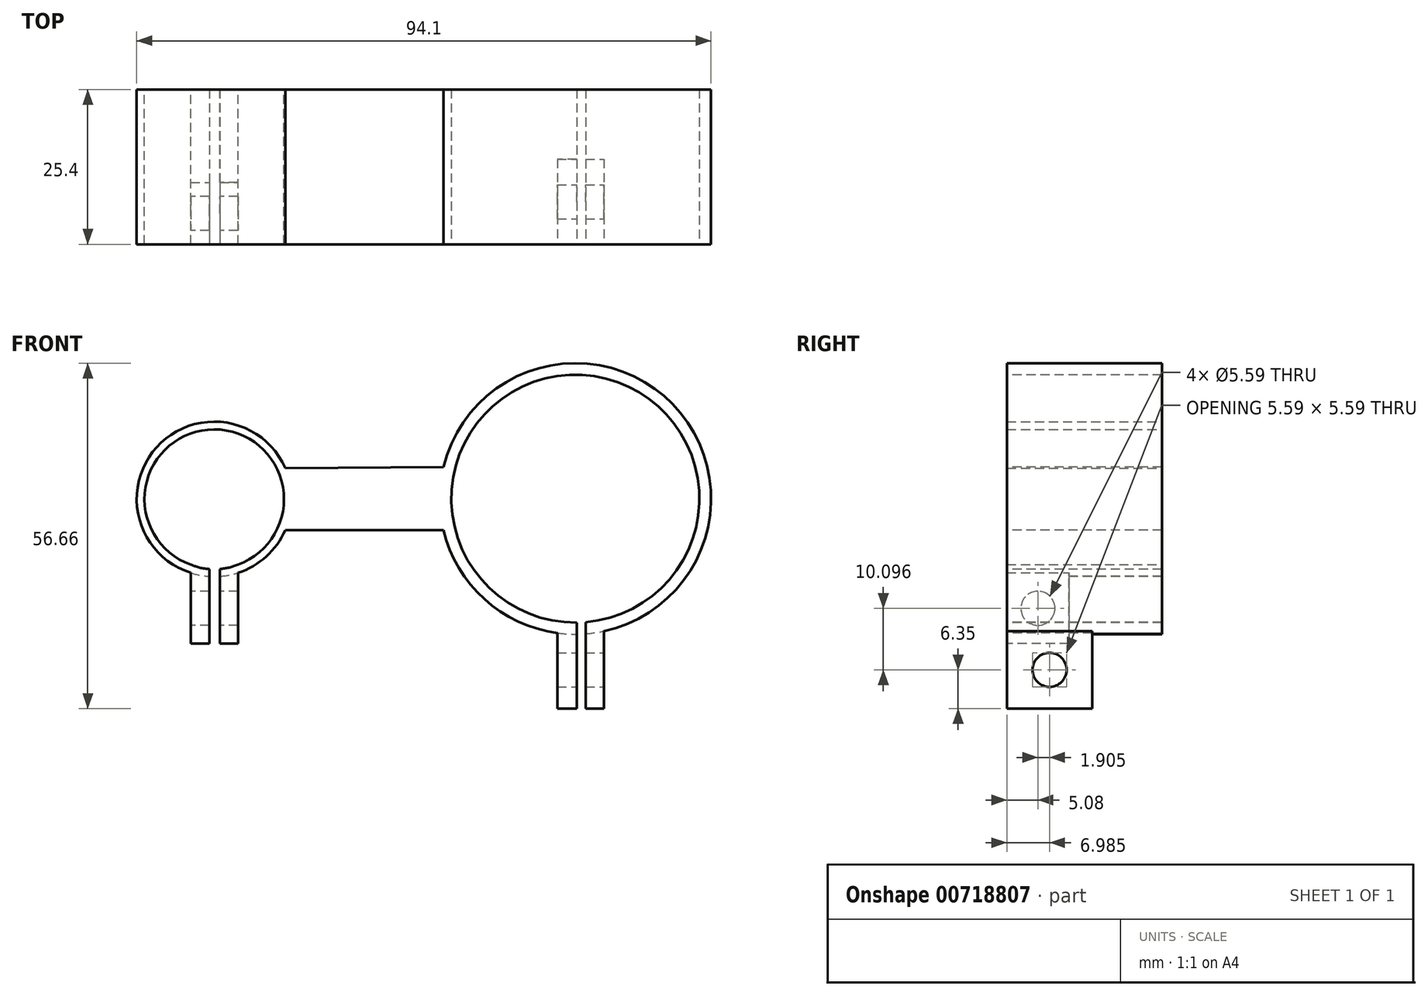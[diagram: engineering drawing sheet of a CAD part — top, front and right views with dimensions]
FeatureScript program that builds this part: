
annotation { "Feature Type Name" : "Feature", "Feature Type Description" : "" }
export const myFeature = defineFeature(function(context is Context, id is Id, definition is map)
    precondition{}
    {
        {
            var Q0;
            Q0=qCreatedBy(makeId("Front.planeOp"),FACE);
            var sketch = newSketch(context, id + "F0", { "sketchPlane" : qUnion([Q0])});
            skCircle(sketch, "E0", {"center": v(0, 0) * mm, "radius": 12.7 * mm});
            skCircle(sketch, "E1", {"center": v(0, 0) * mm, "radius": 11.43 * mm});
            skSolve(sketch);
        }
        {
            var Q0;
            Q0 = qSketchRegion(id + "F0", true);
            extrude(context, id + "F1", {"entities" : qUnion([Q0]), "depth" : 25.4 * mm, "offsetDistance" : 25.4 * mm});
        }
        {
            var Q0;
            Q0=qCreatedBy(makeId("Front.planeOp"),FACE);
            cPlane(context, id + "F2", {"entities" : qUnion([Q0]), "cplaneType" : CPlaneType.OFFSET, "offset" : 25.4 * mm, "width" : 152.4 * mm, "height" : 152.4 * mm});
        }
        {
            var Q0;
            Q0=qCreatedBy(id+"F2.planeOp",FACE);
            var sketch = newSketch(context, id + "F3", { "sketchPlane" : qUnion([Q0])});
            skLineSegment(sketch, "E2", {"start": v(10.6, 5.08) * mm, "end": v(38.72, 5.3) * mm});
            skLineSegment(sketch, "E3", {"start": v(38.68, -5.08) * mm, "end": v(10.4, -5.08) * mm});
            skArc(sketch, "E4", {"start": v(10.4, -5.08) * mm, "mid": v(11.82, -0.02) * mm, "end": v(10.6, 5.08) * mm});
            skPoint(sketch, "E5.orphan", {"position": v(0, -5.08) * mm});
            skArc(sketch, "E6", {"start": v(38.72, 5.3) * mm, "mid": v(37.32, 0.11) * mm, "end": v(38.68, -5.08) * mm});
            skPoint(sketch, "E7.orphan", {"position": v(48.12, -5.08) * mm});
            skLineSegment(sketch, "E8", {"start": v(0, 0) * mm, "end": v(36.95, 0.04) * mm});
            skCircle(sketch, "E9", {"center": v(59.18, 0.07) * mm, "radius": 22.23 * mm});
            skLineSegment(sketch, "E10", {"start": v(37.57, 5.28) * mm, "end": v(38.72, 5.3) * mm});
            skCircle(sketch, "E11", {"center": v(59.18, 0.07) * mm, "radius": 20.32 * mm});
            skSolve(sketch);
        }
        {
            var Q0;
            Q0 = qSketchRegion(id + "F3", true);
            extrude(context, id + "F4", {"entities" : qUnion([Q0]), "oppositeDirection" : true, "depth" : 25.4 * mm, "offsetDistance" : 25.4 * mm});
        }
        {
            var Q0;
            Q0=qCreatedBy(id+"F2.planeOp",FACE);
            var sketch = newSketch(context, id + "F5", { "sketchPlane" : qUnion([Q0])});
            skLineSegment(sketch, "E12", {"start": v(0.94, 1.67) * mm, "end": v(-0.8, 1.67) * mm});
            skLineSegment(sketch, "E13", {"start": v(-0.8, 1.67) * mm, "end": v(-0.8, -23.73) * mm});
            skLineSegment(sketch, "E14", {"start": v(0.94, -23.73) * mm, "end": v(0.94, 1.67) * mm});
            skLineSegment(sketch, "E15", {"start": v(-0.8, 1.67) * mm, "end": v(-3.86, 1.67) * mm});
            skLineSegment(sketch, "E16", {"start": v(-3.86, 1.67) * mm, "end": v(0.94, 1.67) * mm});
            skLineSegment(sketch, "E17", {"start": v(0.94, 1.67) * mm, "end": v(3.9, 1.67) * mm});
            skLineSegment(sketch, "E18", {"start": v(3.9, 1.67) * mm, "end": v(3.9, -23.73) * mm});
            skLineSegment(sketch, "E19", {"start": v(3.9, -23.73) * mm, "end": v(0.94, -23.73) * mm});
            skLineSegment(sketch, "E20", {"start": v(-3.86, 1.67) * mm, "end": v(-3.86, -23.73) * mm});
            skLineSegment(sketch, "E21", {"start": v(-3.86, -23.73) * mm, "end": v(-0.8, -23.73) * mm});
            skLineSegment(sketch, "E22", {"start": v(3.9, -11.03) * mm, "end": v(3.9, -23.73) * mm});
            skSolve(sketch);
        }
        {
            var Q0;
            Q0 = qSketchRegion(id + "F5", true);
            extrude(context, id + "F6", {"entities" : qUnion([Q0]), "operationType" : NewBodyOperationType.ADD, "oppositeDirection" : true, "depth" : 10.16 * mm, "offsetDistance" : 25.4 * mm});
        }
        {
            var Q0;
            Q0=makeQuery(id+"F6.boolean.opBoolean","MERGE",FACE,{"derivedFrom":[makeQuery(id+"F1.opExtrude","CAP_FACE",FACE,{"disambiguationData":[OSD([sQuery(id+"F0.wireOp",EDGE,"E0"),sQuery(id+"F0.wireOp",EDGE,"E1")])],"isStart":false}),makeQuery(id+"F6.opExtrude","CAP_FACE",FACE,{"disambiguationData":[OSD([sQuery(id+"F5.wireOp",EDGE,"E13"),sQuery(id+"F5.wireOp",EDGE,"E16"),sQuery(id+"F5.wireOp",EDGE,"E20"),sQuery(id+"F5.wireOp",EDGE,"E21")])],"isStart":true}),makeQuery(id+"F6.opExtrude","CAP_FACE",FACE,{"disambiguationData":[OSD([sQuery(id+"F5.wireOp",EDGE,"E14"),sQuery(id+"F5.wireOp",EDGE,"E17"),sQuery(id+"F5.wireOp",EDGE,"E18"),sQuery(id+"F5.wireOp",EDGE,"E19")])],"isStart":true})]});
            var sketch = newSketch(context, id + "F7", { "sketchPlane" : qUnion([Q0])});
            skLineSegment(sketch, "E23", {"start": v(-3.86, -10.76) * mm, "end": v(3.9, -10.75) * mm});
            skLineSegment(sketch, "E24", {"start": v(0.94, -12.67) * mm, "end": v(-0.8, -12.68) * mm});
            skLineSegment(sketch, "E25", {"start": v(-3.86, -10.76) * mm, "end": v(-3.86, 6.54) * mm});
            skLineSegment(sketch, "E26", {"start": v(-3.86, 6.54) * mm, "end": v(3.9, 6.82) * mm});
            skLineSegment(sketch, "E27", {"start": v(3.9, 6.82) * mm, "end": v(3.9, -10.75) * mm});
            skLineSegment(sketch, "E28", {"start": v(-0.8, -10.75) * mm, "end": v(-0.8, -12.68) * mm});
            skLineSegment(sketch, "E29", {"start": v(0.94, -10.75) * mm, "end": v(0.94, -11.4) * mm});
            skLineSegment(sketch, "E30", {"start": v(0.94, -12.67) * mm, "end": v(0.94, -11.4) * mm});
            skSolve(sketch);
        }
        {
            var Q0;
            Q0 = qSketchRegion(id + "F7", true);
            extrude(context, id + "F8", {"entities" : qUnion([Q0]), "operationType" : NewBodyOperationType.REMOVE, "oppositeDirection" : true, "depth" : 30.23 * mm, "offsetDistance" : 25.4 * mm});
        }
        {
            var Q0;
            Q0 = qSketchRegion(id + "F7", true);
            extrude(context, id + "F9", {"entities" : qUnion([Q0]), "operationType" : NewBodyOperationType.REMOVE, "oppositeDirection" : true, "depth" : 25.4 * mm, "offsetDistance" : 25.4 * mm});
        }
        {
            var Q0;
            {var subQ1=sQuery(id+"F5.wireOp",EDGE,"E20");var subQ4=sQuery(id+"F0.wireOp",EDGE,"E0");Q0=makeQuery(id+"F6.boolean.opBoolean","SPLIT",FACE,{"disambiguationData":[TD([makeQuery(id+"F1.opExtrude","SWEPT_FACE",FACE,{"disambiguationData":[OSD([subQ4])]})])],"derivedFrom":makeQuery(id+"F6.opExtrude","SWEPT_FACE",FACE,{"disambiguationData":[OSD([subQ1])]})});}
            var sketch = newSketch(context, id + "F10", { "sketchPlane" : qUnion([Q0])});
            skCircle(sketch, "E31", {"center": v(20.32, -17.91) * mm, "radius": 2.8 * mm});
            skPoint(sketch, "E31.centerSnap0", {"position": v(20.32, -23.73) * mm});
            skPoint(sketch, "E31.centerSnap1", {"position": v(15.24, -17.91) * mm});
            skSolve(sketch);
        }
        {
            var Q0;
            Q0 = qSketchRegion(id + "F10", true);
            extrude(context, id + "F11", {"entities" : qUnion([Q0]), "operationType" : NewBodyOperationType.REMOVE, "oppositeDirection" : true, "depth" : 25.4 * mm, "offsetDistance" : 25.4 * mm});
        }
        {
            var Q0;
            Q0=makeQuery(id+"F1.opExtrude","SWEPT_BODY",BODY,{"disambiguationData":[OSD([sQuery(id+"F0.wireOp",EDGE,"E0"),sQuery(id+"F0.wireOp",EDGE,"E1")])]});
            var Q1;
            Q1=makeQuery(id+"F4.opExtrude","SWEPT_BODY",BODY,{"disambiguationData":[OSD([sQuery(id+"F3.wireOp",EDGE,"E2"),sQuery(id+"F3.wireOp",EDGE,"E3"),sQuery(id+"F3.wireOp",EDGE,"E4"),sQuery(id+"F3.wireOp",EDGE,"E9"),sQuery(id+"F3.wireOp",EDGE,"E11")])]});
            booleanBodies(context, id + "F12", {"operationType" : BooleanOperationType.UNION, "tools" : qUnion([Q0, Q1])});
        }
        {
            var Q0;
            Q0=makeQuery(id+"F12.opBoolean","MERGE",FACE,{"derivedFrom":[makeQuery(id+"F4.opExtrude","CAP_FACE",FACE,{"disambiguationData":[OSD([sQuery(id+"F3.wireOp",EDGE,"E2"),sQuery(id+"F3.wireOp",EDGE,"E3"),sQuery(id+"F3.wireOp",EDGE,"E4"),sQuery(id+"F3.wireOp",EDGE,"E9"),sQuery(id+"F3.wireOp",EDGE,"E11")])],"isStart":true}),makeQuery(id+"F6.boolean.opBoolean","MERGE",FACE,{"derivedFrom":[makeQuery(id+"F1.opExtrude","CAP_FACE",FACE,{"disambiguationData":[OSD([sQuery(id+"F0.wireOp",EDGE,"E0"),sQuery(id+"F0.wireOp",EDGE,"E1")])],"isStart":false}),makeQuery(id+"F6.opExtrude","CAP_FACE",FACE,{"disambiguationData":[OSD([sQuery(id+"F5.wireOp",EDGE,"E13"),sQuery(id+"F5.wireOp",EDGE,"E16"),sQuery(id+"F5.wireOp",EDGE,"E20"),sQuery(id+"F5.wireOp",EDGE,"E21")])],"isStart":true}),makeQuery(id+"F6.opExtrude","CAP_FACE",FACE,{"disambiguationData":[OSD([sQuery(id+"F5.wireOp",EDGE,"E14"),sQuery(id+"F5.wireOp",EDGE,"E17"),sQuery(id+"F5.wireOp",EDGE,"E18"),sQuery(id+"F5.wireOp",EDGE,"E19")])],"isStart":true})]})]});
            var sketch = newSketch(context, id + "F13", { "sketchPlane" : qUnion([Q0])});
            skLineSegment(sketch, "E32", {"start": v(59.39, 1.2) * mm, "end": v(60.86, 1.2) * mm});
            skLineSegment(sketch, "E33", {"start": v(60.86, 1.2) * mm, "end": v(60.86, -34.36) * mm});
            skLineSegment(sketch, "E34", {"start": v(60.86, -34.36) * mm, "end": v(63.83, -34.36) * mm});
            skLineSegment(sketch, "E35", {"start": v(63.83, -34.36) * mm, "end": v(63.83, 1.2) * mm});
            skLineSegment(sketch, "E36", {"start": v(63.83, 1.2) * mm, "end": v(59.39, 1.2) * mm});
            skLineSegment(sketch, "E37", {"start": v(59.39, 1.2) * mm, "end": v(59.39, -34.36) * mm});
            skLineSegment(sketch, "E38", {"start": v(59.39, -34.36) * mm, "end": v(56.21, -34.36) * mm});
            skLineSegment(sketch, "E39", {"start": v(56.21, -34.36) * mm, "end": v(56.21, 1.2) * mm});
            skLineSegment(sketch, "E40", {"start": v(56.21, 1.2) * mm, "end": v(59.39, 1.2) * mm});
            skLineSegment(sketch, "E41", {"start": v(63.83, -21.66) * mm, "end": v(63.83, -34.36) * mm});
            skSolve(sketch);
        }
        {
            var Q0;
            Q0 = qSketchRegion(id + "F13", true);
            extrude(context, id + "F14", {"entities" : qUnion([Q0]), "operationType" : NewBodyOperationType.ADD, "oppositeDirection" : true, "depth" : 13.97 * mm, "offsetDistance" : 25.4 * mm});
        }
        {
            var Q0;
            {var subQ0=sQuery(id+"F3.wireOp",EDGE,"E9");var subQ1=sQuery(id+"F13.wireOp",EDGE,"E41");var subQ3=sQuery(id+"F13.wireOp",EDGE,"E35");Q0=makeQuery(id+"F14.boolean.opBoolean","SPLIT",FACE,{"disambiguationData":[TD([makeQuery(id+"F4.opExtrude","SWEPT_FACE",FACE,{"disambiguationData":[OSD([subQ0])]})])],"derivedFrom":makeQuery(id+"F14.opExtrude","SWEPT_FACE",FACE,{"disambiguationData":[OSD([subQ3,subQ1])]})});}
            var sketch = newSketch(context, id + "F15", { "sketchPlane" : qUnion([Q0])});
            skCircle(sketch, "E42", {"center": v(-18.41, -28) * mm, "radius": 2.8 * mm});
            skPoint(sketch, "E42.centerSnap0", {"position": v(-11.43, -28) * mm});
            skPoint(sketch, "E42.centerSnap1", {"position": v(-18.41, -21.66) * mm});
            skSolve(sketch);
        }
        {
            var Q0;
            Q0 = qSketchRegion(id + "F15", true);
            extrude(context, id + "F16", {"entities" : qUnion([Q0]), "operationType" : NewBodyOperationType.REMOVE, "oppositeDirection" : true, "depth" : 25.4 * mm, "offsetDistance" : 25.4 * mm});
        }
        {
            var Q0;
            Q0=makeQuery(id+"F14.boolean.opBoolean","MERGE",FACE,{"derivedFrom":[makeQuery(id+"F12.opBoolean","MERGE",FACE,{"derivedFrom":[makeQuery(id+"F4.opExtrude","CAP_FACE",FACE,{"disambiguationData":[OSD([sQuery(id+"F3.wireOp",EDGE,"E2"),sQuery(id+"F3.wireOp",EDGE,"E3"),sQuery(id+"F3.wireOp",EDGE,"E4"),sQuery(id+"F3.wireOp",EDGE,"E9"),sQuery(id+"F3.wireOp",EDGE,"E11")])],"isStart":true}),makeQuery(id+"F6.boolean.opBoolean","MERGE",FACE,{"derivedFrom":[makeQuery(id+"F1.opExtrude","CAP_FACE",FACE,{"disambiguationData":[OSD([sQuery(id+"F0.wireOp",EDGE,"E0"),sQuery(id+"F0.wireOp",EDGE,"E1")])],"isStart":false}),makeQuery(id+"F6.opExtrude","CAP_FACE",FACE,{"disambiguationData":[OSD([sQuery(id+"F5.wireOp",EDGE,"E13"),sQuery(id+"F5.wireOp",EDGE,"E16"),sQuery(id+"F5.wireOp",EDGE,"E20"),sQuery(id+"F5.wireOp",EDGE,"E21")])],"isStart":true}),makeQuery(id+"F6.opExtrude","CAP_FACE",FACE,{"disambiguationData":[OSD([sQuery(id+"F5.wireOp",EDGE,"E14"),sQuery(id+"F5.wireOp",EDGE,"E17"),sQuery(id+"F5.wireOp",EDGE,"E18"),sQuery(id+"F5.wireOp",EDGE,"E19"),sQuery(id+"F5.wireOp",EDGE,"E22")])],"isStart":true})]})]}),makeQuery(id+"F14.opExtrude","CAP_FACE",FACE,{"disambiguationData":[OSD([sQuery(id+"F13.wireOp",EDGE,"E33"),sQuery(id+"F13.wireOp",EDGE,"E34"),sQuery(id+"F13.wireOp",EDGE,"E35"),sQuery(id+"F13.wireOp",EDGE,"E36"),sQuery(id+"F13.wireOp",EDGE,"E41")])],"isStart":true}),makeQuery(id+"F14.opExtrude","CAP_FACE",FACE,{"disambiguationData":[OSD([sQuery(id+"F13.wireOp",EDGE,"E37"),sQuery(id+"F13.wireOp",EDGE,"E38"),sQuery(id+"F13.wireOp",EDGE,"E39"),sQuery(id+"F13.wireOp",EDGE,"E40")])],"isStart":true})]});
            var sketch = newSketch(context, id + "F17", { "sketchPlane" : qUnion([Q0])});
            skArc(sketch, "E43", {"start": v(56.21, -20.03) * mm, "mid": v(58.31, 20.37) * mm, "end": v(63.83, -19.7) * mm});
            skLineSegment(sketch, "E44", {"start": v(59.39, -22.15) * mm, "end": v(59.39, -20.25) * mm});
            skLineSegment(sketch, "E45", {"start": v(59.39, -20.25) * mm, "end": v(59.39, -22.15) * mm});
            skLineSegment(sketch, "E46", {"start": v(59.39, -22.15) * mm, "end": v(60.86, -22.09) * mm});
            skLineSegment(sketch, "E47", {"start": v(60.86, -22.09) * mm, "end": v(60.86, -20.18) * mm});
            skLineSegment(sketch, "E48", {"start": v(56.21, -20.03) * mm, "end": v(56.21, 1.2) * mm});
            skLineSegment(sketch, "E49", {"start": v(56.21, 1.2) * mm, "end": v(63.83, 1.2) * mm});
            skLineSegment(sketch, "E50", {"start": v(63.83, 1.2) * mm, "end": v(63.83, -19.7) * mm});
            skLineSegment(sketch, "E51", {"start": v(59.39, -22.15) * mm, "end": v(59.39, -22.38) * mm});
            skLineSegment(sketch, "E52", {"start": v(59.39, -22.38) * mm, "end": v(60.86, -22.38) * mm});
            skLineSegment(sketch, "E53", {"start": v(60.86, -22.38) * mm, "end": v(60.86, -22.09) * mm});
            skLineSegment(sketch, "E54", {"start": v(59.39, 1.2) * mm, "end": v(59.39, -20.25) * mm});
            skLineSegment(sketch, "E55", {"start": v(60.86, 1.2) * mm, "end": v(60.86, -20.18) * mm});
            skArc(sketch, "E56", {"start": v(56.21, -20.03) * mm, "mid": v(60.04, -20.23) * mm, "end": v(63.83, -19.7) * mm});
            skSolve(sketch);
        }
        {
            var Q0;
            Q0 = qSketchRegion(id + "F17", true);
            extrude(context, id + "F18", {"entities" : qUnion([Q0]), "operationType" : NewBodyOperationType.REMOVE, "oppositeDirection" : true, "depth" : 30.73 * mm, "offsetDistance" : 25.4 * mm});
        }
        {
            var Q0;
            Q0=makeQuery(id+"F14.boolean.opBoolean","MERGE",FACE,{"derivedFrom":[makeQuery(id+"F12.opBoolean","MERGE",FACE,{"derivedFrom":[makeQuery(id+"F4.opExtrude","CAP_FACE",FACE,{"disambiguationData":[OSD([sQuery(id+"F3.wireOp",EDGE,"E2"),sQuery(id+"F3.wireOp",EDGE,"E3"),sQuery(id+"F3.wireOp",EDGE,"E4"),sQuery(id+"F3.wireOp",EDGE,"E9"),sQuery(id+"F3.wireOp",EDGE,"E11")])],"isStart":true}),makeQuery(id+"F6.boolean.opBoolean","MERGE",FACE,{"derivedFrom":[makeQuery(id+"F1.opExtrude","CAP_FACE",FACE,{"disambiguationData":[OSD([sQuery(id+"F0.wireOp",EDGE,"E0"),sQuery(id+"F0.wireOp",EDGE,"E1")])],"isStart":false}),makeQuery(id+"F6.opExtrude","CAP_FACE",FACE,{"disambiguationData":[OSD([sQuery(id+"F5.wireOp",EDGE,"E13"),sQuery(id+"F5.wireOp",EDGE,"E16"),sQuery(id+"F5.wireOp",EDGE,"E20"),sQuery(id+"F5.wireOp",EDGE,"E21")])],"isStart":true}),makeQuery(id+"F6.opExtrude","CAP_FACE",FACE,{"disambiguationData":[OSD([sQuery(id+"F5.wireOp",EDGE,"E14"),sQuery(id+"F5.wireOp",EDGE,"E17"),sQuery(id+"F5.wireOp",EDGE,"E18"),sQuery(id+"F5.wireOp",EDGE,"E19"),sQuery(id+"F5.wireOp",EDGE,"E22")])],"isStart":true})]})]}),makeQuery(id+"F14.opExtrude","CAP_FACE",FACE,{"disambiguationData":[OSD([sQuery(id+"F13.wireOp",EDGE,"E33"),sQuery(id+"F13.wireOp",EDGE,"E34"),sQuery(id+"F13.wireOp",EDGE,"E35"),sQuery(id+"F13.wireOp",EDGE,"E36"),sQuery(id+"F13.wireOp",EDGE,"E41")])],"isStart":true}),makeQuery(id+"F14.opExtrude","CAP_FACE",FACE,{"disambiguationData":[OSD([sQuery(id+"F13.wireOp",EDGE,"E37"),sQuery(id+"F13.wireOp",EDGE,"E38"),sQuery(id+"F13.wireOp",EDGE,"E39"),sQuery(id+"F13.wireOp",EDGE,"E40")])],"isStart":true})]});
            var sketch = newSketch(context, id + "F19", { "sketchPlane" : qUnion([Q0])});
            skArc(sketch, "E57", {"start": v(-3.86, -10.76) * mm, "mid": v(0.02, -11.52) * mm, "end": v(3.9, -10.75) * mm});
            skLineSegment(sketch, "E58", {"start": v(-3.86, -10.76) * mm, "end": v(-3.86, -9.75) * mm});
            skLineSegment(sketch, "E59", {"start": v(-3.86, -9.75) * mm, "end": v(3.9, -9.73) * mm});
            skLineSegment(sketch, "E60", {"start": v(3.9, -9.73) * mm, "end": v(3.9, -10.75) * mm});
            skSolve(sketch);
        }
        {
            var Q0;
            Q0 = qSketchRegion(id + "F19", true);
            extrude(context, id + "F20", {"entities" : qUnion([Q0]), "operationType" : NewBodyOperationType.REMOVE, "oppositeDirection" : true, "depth" : 40.64 * mm, "offsetDistance" : 25.4 * mm});
        }
        {
            var Q0;
            {var subQ0=sQuery(id+"F5.wireOp",EDGE,"E20");var subQ2=sQuery(id+"F5.wireOp",EDGE,"E19");var subQ3=sQuery(id+"F0.wireOp",EDGE,"E1");var subQ4=makeQuery(id+"F1.opExtrude","SWEPT_FACE",FACE,{"disambiguationData":[OSD([subQ3])]});var subQ6=sQuery(id+"F5.wireOp",EDGE,"E22");var subQ7=sQuery(id+"F5.wireOp",EDGE,"E18");var subQ8=sQuery(id+"F5.wireOp",EDGE,"E17");var subQ9=sQuery(id+"F5.wireOp",EDGE,"E14");var subQ10=makeQuery(id+"F6.opExtrude","CAP_FACE",FACE,{"disambiguationData":[OSD([subQ9,subQ8,subQ7,subQ2,subQ6])],"isStart":true});var subQ11=sQuery(id+"F5.wireOp",EDGE,"E21");var subQ12=sQuery(id+"F5.wireOp",EDGE,"E16");var subQ13=sQuery(id+"F5.wireOp",EDGE,"E13");var subQ14=makeQuery(id+"F6.opExtrude","CAP_FACE",FACE,{"disambiguationData":[OSD([subQ13,subQ12,subQ0,subQ11])],"isStart":true});var subQ16=sQuery(id+"F0.wireOp",EDGE,"E0");var subQ17=makeQuery(id+"F1.opExtrude","CAP_FACE",FACE,{"disambiguationData":[OSD([subQ16,subQ3])],"isStart":false});Q0=makeQuery(id+"F14.boolean.opBoolean","MERGE",FACE,{"derivedFrom":[makeQuery(id+"F12.opBoolean","MERGE",FACE,{"derivedFrom":[makeQuery(id+"F4.opExtrude","CAP_FACE",FACE,{"disambiguationData":[OSD([sQuery(id+"F3.wireOp",EDGE,"E2"),sQuery(id+"F3.wireOp",EDGE,"E3"),sQuery(id+"F3.wireOp",EDGE,"E4"),sQuery(id+"F3.wireOp",EDGE,"E9"),sQuery(id+"F3.wireOp",EDGE,"E11")])],"isStart":true}),makeQuery(id+"F8.boolean.opBoolean","SPLIT",FACE,{"disambiguationData":[TD([subQ4])],"derivedFrom":makeQuery(id+"F6.boolean.opBoolean","MERGE",FACE,{"derivedFrom":[subQ17,subQ14,subQ10]})})]}),makeQuery(id+"F14.opExtrude","CAP_FACE",FACE,{"disambiguationData":[OSD([sQuery(id+"F13.wireOp",EDGE,"E33"),sQuery(id+"F13.wireOp",EDGE,"E34"),sQuery(id+"F13.wireOp",EDGE,"E35"),sQuery(id+"F13.wireOp",EDGE,"E36"),sQuery(id+"F13.wireOp",EDGE,"E41")])],"isStart":true}),makeQuery(id+"F14.opExtrude","CAP_FACE",FACE,{"disambiguationData":[OSD([sQuery(id+"F13.wireOp",EDGE,"E37"),sQuery(id+"F13.wireOp",EDGE,"E38"),sQuery(id+"F13.wireOp",EDGE,"E39"),sQuery(id+"F13.wireOp",EDGE,"E40")])],"isStart":true})]});}
            var sketch = newSketch(context, id + "F21", { "sketchPlane" : qUnion([Q0])});
            skLineSegment(sketch, "E61", {"start": v(-0.8, -11.49) * mm, "end": v(-0.8, -13.05) * mm});
            skLineSegment(sketch, "E62", {"start": v(-0.8, -13.05) * mm, "end": v(0.94, -13.05) * mm});
            skLineSegment(sketch, "E63", {"start": v(0.94, -13.05) * mm, "end": v(0.94, -11.48) * mm});
            skLineSegment(sketch, "E64", {"start": v(0.94, -11.48) * mm, "end": v(-0.8, -11.49) * mm});
            skSolve(sketch);
        }
        {
            var Q0;
            Q0 = qSketchRegion(id + "F21", true);
            extrude(context, id + "F22", {"entities" : qUnion([Q0]), "operationType" : NewBodyOperationType.REMOVE, "oppositeDirection" : true, "depth" : 25.4 * mm, "offsetDistance" : 25.4 * mm});
        }
    });
